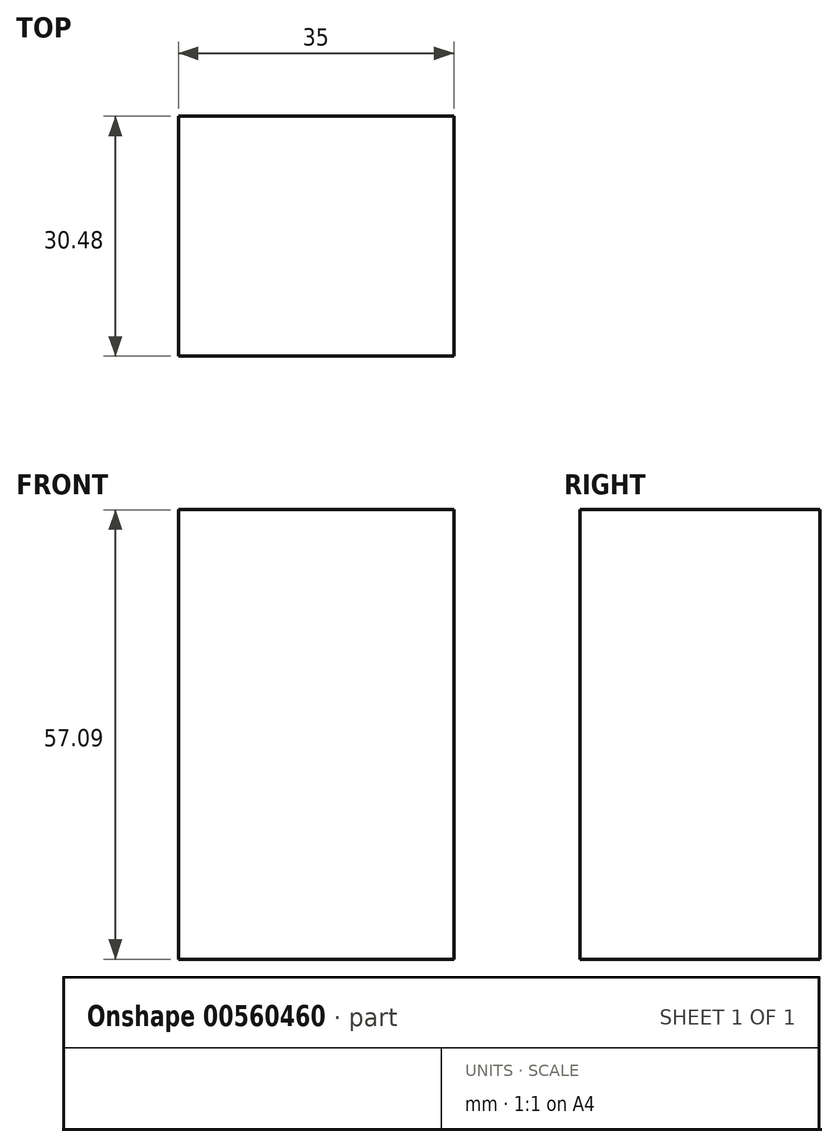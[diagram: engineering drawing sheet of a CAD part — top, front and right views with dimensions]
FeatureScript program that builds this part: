
annotation { "Feature Type Name" : "Feature", "Feature Type Description" : "" }
export const myFeature = defineFeature(function(context is Context, id is Id, definition is map)
    precondition{}
    {
        {
            var Q0;
            Q0=qCreatedBy(makeId("Front.planeOp"),FACE);
            var sketch = newSketch(context, id + "F0", { "sketchPlane" : qUnion([Q0])});
            skLineSegment(sketch, "E0.bottom", {"start": v(-59.17, 57.1) * mm, "end": v(-24.17, 57.1) * mm});
            skLineSegment(sketch, "E0.top", {"start": v(-59.17, 0) * mm, "end": v(-24.17, 0) * mm});
            skLineSegment(sketch, "E0.left", {"start": v(-59.17, 57.1) * mm, "end": v(-59.17, 0) * mm});
            skLineSegment(sketch, "E0.right", {"start": v(-24.17, 57.1) * mm, "end": v(-24.17, 0) * mm});
            skSolve(sketch);
        }
        {
            var Q0;
            Q0=makeQuery(id+"F0.imprint","IMPRINT",FACE,{"disambiguationData":[TD([[makeQuery(id+"F0.imprint","IMPRINT",EDGE,{"derivedFrom":sQuery(id+"F0.wireOp",EDGE,"E0.bottom")}),-1.0]])]});
            extrude(context, id + "F1", {"entities" : qUnion([Q0]), "depth" : 30.48 * mm, "offsetDistance" : 30.48 * mm});
        }
    });
